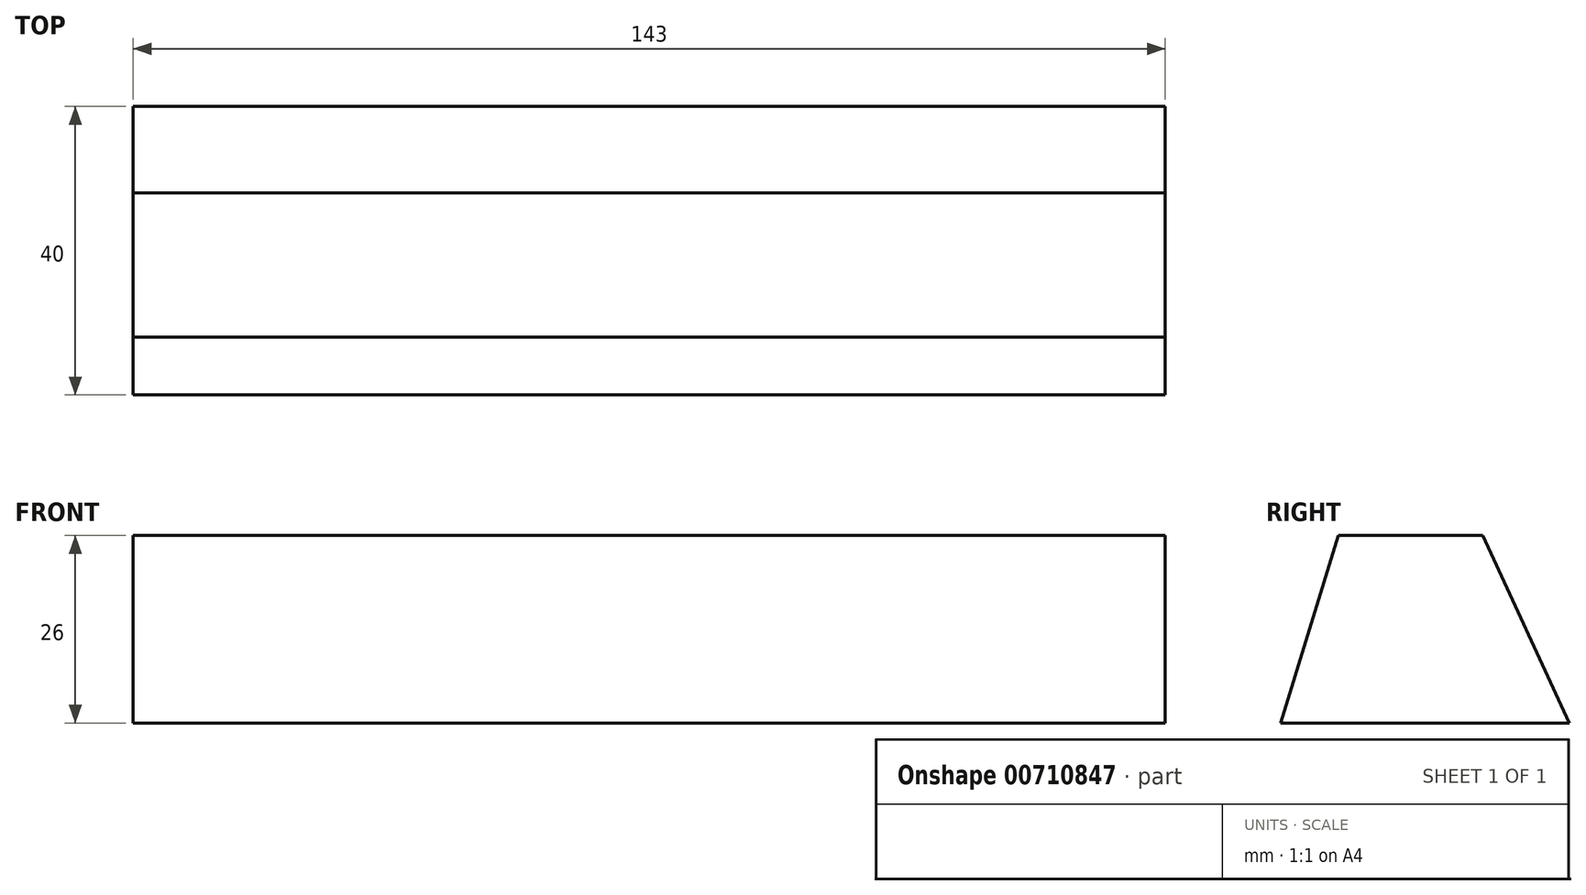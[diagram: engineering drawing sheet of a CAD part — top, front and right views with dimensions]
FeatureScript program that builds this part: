
annotation { "Feature Type Name" : "Feature", "Feature Type Description" : "" }
export const myFeature = defineFeature(function(context is Context, id is Id, definition is map)
    precondition{}
    {
        {
            var Q0;
            Q0=qCreatedBy(makeId("Right.planeOp"),FACE);
            var sketch = newSketch(context, id + "F0", { "sketchPlane" : qUnion([Q0])});
            skLineSegment(sketch, "E0", {"start": v(-12, 26) * mm, "end": v(-20, 0) * mm});
            skLineSegment(sketch, "E1", {"start": v(-20, 0) * mm, "end": v(20, 0) * mm});
            skLineSegment(sketch, "E2", {"start": v(20, 0) * mm, "end": v(8, 26) * mm});
            skLineSegment(sketch, "E3", {"start": v(8, 26) * mm, "end": v(-12, 26) * mm});
            skSolve(sketch);
        }
        {
            var Q0;
            Q0=makeQuery(id+"F0.imprint","IMPRINT",FACE,{"disambiguationData":[TD([[makeQuery(id+"F0.imprint","IMPRINT",EDGE,{"derivedFrom":sQuery(id+"F0.wireOp",EDGE,"E0")}),1.0]])]});
            extrude(context, id + "F1", {"entities" : qUnion([Q0]), "endBound" : BoundingType.SYMMETRIC, "depth" : 143 * mm, "offsetDistance" : 25 * mm});
        }
    });
